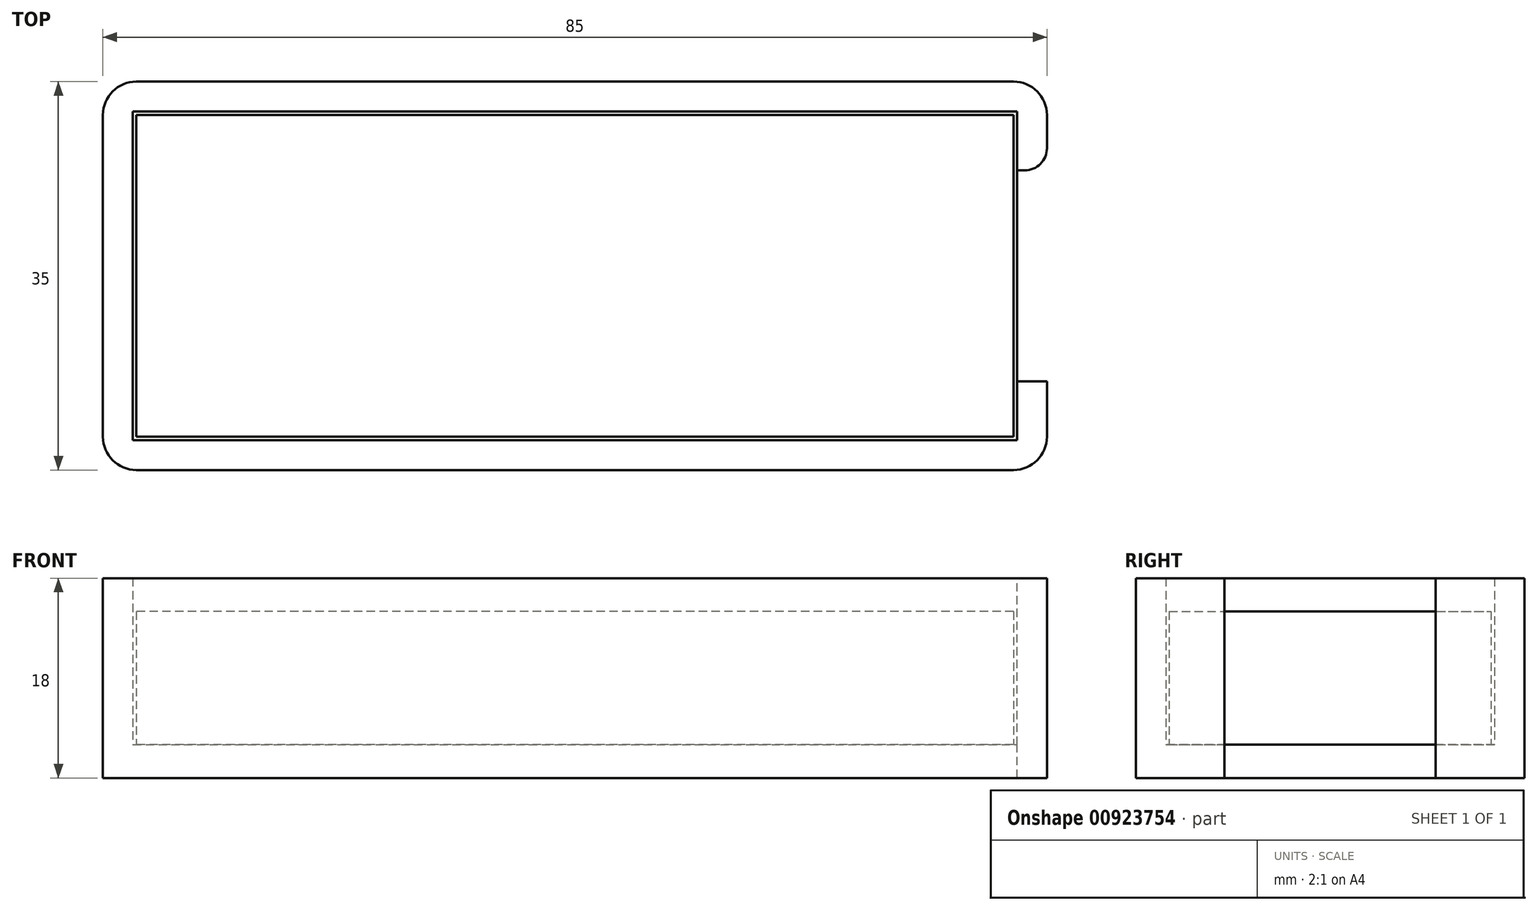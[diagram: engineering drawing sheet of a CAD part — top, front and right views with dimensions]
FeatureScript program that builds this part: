
annotation { "Feature Type Name" : "Feature", "Feature Type Description" : "" }
export const myFeature = defineFeature(function(context is Context, id is Id, definition is map)
    precondition{}
    {
        {
            var Q0;
            Q0=qCreatedBy(makeId("Top.planeOp"),FACE);
            var sketch = newSketch(context, id + "F0", { "sketchPlane" : qUnion([Q0])});
            skLineSegment(sketch, "E0.bottom", {"start": v(39.5, -14.5) * mm, "end": v(-39.5, -14.5) * mm});
            skLineSegment(sketch, "E0.top", {"start": v(39.5, 14.5) * mm, "end": v(-39.5, 14.5) * mm});
            skLineSegment(sketch, "E0.left", {"start": v(39.5, -14.5) * mm, "end": v(39.5, 14.5) * mm});
            skLineSegment(sketch, "E0.right", {"start": v(-39.5, -14.5) * mm, "end": v(-39.5, 14.5) * mm});
            skPoint(sketch, "E0.middle", {"position": v(0, 0) * mm});
            skSolve(sketch);
        }
        {
            var Q0;
            Q0 = qSketchRegion(id + "F0", true);
            extrude(context, id + "F1", {"entities" : qUnion([Q0]), "depth" : 12 * mm, "offsetDistance" : 25 * mm});
        }
        {
            var Q0;
            Q0=qCreatedBy(makeId("Top.planeOp"),FACE);
            var sketch = newSketch(context, id + "F2", { "sketchPlane" : qUnion([Q0])});
            skLineSegment(sketch, "E1.bottom", {"start": v(42.5, -17.5) * mm, "end": v(-42.5, -17.5) * mm});
            skLineSegment(sketch, "E1.top", {"start": v(42.5, 17.5) * mm, "end": v(-42.5, 17.5) * mm});
            skLineSegment(sketch, "E1.left", {"start": v(42.5, -17.5) * mm, "end": v(42.5, 17.5) * mm});
            skLineSegment(sketch, "E1.right", {"start": v(-42.5, -17.5) * mm, "end": v(-42.5, 17.5) * mm});
            skPoint(sketch, "E1.middle", {"position": v(0, 0) * mm});
            skLineSegment(sketch, "E2.bottom", {"start": v(-39.5, -14.5) * mm, "end": v(39.5, -14.5) * mm});
            skLineSegment(sketch, "E2.top", {"start": v(-39.5, 14.5) * mm, "end": v(39.5, 14.5) * mm});
            skLineSegment(sketch, "E2.left", {"start": v(-39.5, -14.5) * mm, "end": v(-39.5, 14.5) * mm});
            skLineSegment(sketch, "E2.right", {"start": v(39.5, -14.5) * mm, "end": v(39.5, 14.5) * mm});
            skLineSegment(sketch, "E3.0", {"start": v(39.8, -14.8) * mm, "end": v(39.8, 14.8) * mm});
            skLineSegment(sketch, "E3.1", {"start": v(-39.8, -14.8) * mm, "end": v(39.8, -14.8) * mm});
            skLineSegment(sketch, "E3.2", {"start": v(-39.8, 14.8) * mm, "end": v(-39.8, -14.8) * mm});
            skLineSegment(sketch, "E3.3", {"start": v(39.8, 14.8) * mm, "end": v(-39.8, 14.8) * mm});
            skSolve(sketch);
        }
        {
            var Q0;
            Q0 = qSketchRegion(id + "F2", true);
            extrude(context, id + "F3", {"entities" : qUnion([Q0]), "depth" : 15 * mm, "offsetDistance" : 25 * mm});
        }
        {
            var Q0;
            Q0=makeQuery(id+"F3.opExtrude","CAP_FACE",FACE,{"disambiguationData":[OSD([sQuery(id+"F2.wireOp",EDGE,"E1.bottom"),sQuery(id+"F2.wireOp",EDGE,"E1.top"),sQuery(id+"F2.wireOp",EDGE,"E1.left"),sQuery(id+"F2.wireOp",EDGE,"E1.right"),sQuery(id+"F2.wireOp",EDGE,"E3.0"),sQuery(id+"F2.wireOp",EDGE,"E3.1"),sQuery(id+"F2.wireOp",EDGE,"E3.2"),sQuery(id+"F2.wireOp",EDGE,"E3.3")])],"isStart":true});
            var sketch = newSketch(context, id + "F4", { "sketchPlane" : qUnion([Q0])});
            skLineSegment(sketch, "E4.bottom", {"start": v(-42.5, -17.5) * mm, "end": v(42.5, -17.5) * mm});
            skLineSegment(sketch, "E4.top", {"start": v(-42.5, 17.5) * mm, "end": v(42.5, 17.5) * mm});
            skLineSegment(sketch, "E4.left", {"start": v(-42.5, -17.5) * mm, "end": v(-42.5, 17.5) * mm});
            skLineSegment(sketch, "E4.right", {"start": v(42.5, -17.5) * mm, "end": v(42.5, 17.5) * mm});
            skPoint(sketch, "E4.middle", {"position": v(0, 0) * mm});
            skSolve(sketch);
        }
        {
            var Q0;
            Q0 = qSketchRegion(id + "F4", true);
            extrude(context, id + "F5", {"entities" : qUnion([Q0]), "operationType" : NewBodyOperationType.ADD, "depth" : 3 * mm, "offsetDistance" : 25 * mm});
        }
        {
            var Q0;
            Q0=makeQuery(id+"F3.opExtrude","CAP_FACE",FACE,{"disambiguationData":[OSD([sQuery(id+"F2.wireOp",EDGE,"E1.bottom"),sQuery(id+"F2.wireOp",EDGE,"E1.top"),sQuery(id+"F2.wireOp",EDGE,"E1.left"),sQuery(id+"F2.wireOp",EDGE,"E1.right"),sQuery(id+"F2.wireOp",EDGE,"E3.0"),sQuery(id+"F2.wireOp",EDGE,"E3.1"),sQuery(id+"F2.wireOp",EDGE,"E3.2"),sQuery(id+"F2.wireOp",EDGE,"E3.3")])],"isStart":false});
            var sketch = newSketch(context, id + "F6", { "sketchPlane" : qUnion([Q0])});
            skLineSegment(sketch, "E5.bottom", {"start": v(42.5, -17.5) * mm, "end": v(39.8, -17.5) * mm});
            skLineSegment(sketch, "E5.top", {"start": v(42.5, -9.5) * mm, "end": v(39.8, -9.5) * mm});
            skLineSegment(sketch, "E5.left", {"start": v(42.5, -17.5) * mm, "end": v(42.5, -9.5) * mm});
            skLineSegment(sketch, "E5.right", {"start": v(39.8, -17.5) * mm, "end": v(39.8, -9.5) * mm});
            skLineSegment(sketch, "E6.MirrorCS", {"start": v(42.5, 17.5) * mm, "end": v(39.8, 17.5) * mm});
            skLineSegment(sketch, "E7.MirrorCS", {"start": v(39.8, 17.5) * mm, "end": v(39.8, 9.5) * mm});
            skLineSegment(sketch, "E8.MirrorCS", {"start": v(42.5, 17.5) * mm, "end": v(42.5, 9.5) * mm});
            skLineSegment(sketch, "E9.MirrorCS", {"start": v(42.5, 9.5) * mm, "end": v(39.8, 9.5) * mm});
            skSolve(sketch);
        }
        {
            var Q0;
            {var subQ0=sQuery(id+"F6.wireOp",EDGE,"E5.top");Q0=makeQuery(id+"F6.imprint","IMPRINT",FACE,{"disambiguationData":[TD([[makeQuery(id+"F6.imprint","IMPRINT",EDGE,{"derivedFrom":subQ0}),-1.0]])]});}
            extrude(context, id + "F7", {"entities" : qUnion([Q0]), "operationType" : NewBodyOperationType.REMOVE, "oppositeDirection" : true, "depth" : 25 * mm, "offsetDistance" : 25 * mm});
        }
        {
            var Q0;
            Q0=makeQuery(id+"F7.boolean.opBoolean","COPY",EDGE,{"derivedFrom":makeQuery(id+"F7.opExtrude","SWEPT_EDGE",EDGE,{"disambiguationData":[OSD([sQuery(id+"F2.wireOp",EDGE,"E1.left"),sQuery(id+"F6.wireOp",EDGE,"E5.top"),sQuery(id+"F6.wireOp",EDGE,"E5.left")])]})});
            var Q1;
            Q1=makeQuery(id+"F7.boolean.opBoolean","COPY",EDGE,{"derivedFrom":makeQuery(id+"F7.opExtrude","SWEPT_EDGE",EDGE,{"disambiguationData":[OSD([sQuery(id+"F2.wireOp",EDGE,"E1.left"),sQuery(id+"F6.wireOp",EDGE,"E8.MirrorCS"),sQuery(id+"F6.wireOp",EDGE,"E9.MirrorCS")])]})});
            fillet(context, id + "F8", {"entities" : qUnion([Q0, Q1]), "radius" : 2 * mm, "tangentPropagation" : true, "allowEdgeOverflow" : false});
        }
        {
            var Q0;
            Q0=makeQuery(id+"F5.boolean.opBoolean","MERGE",EDGE,{"derivedFrom":[makeQuery(id+"F3.opExtrude","SWEPT_EDGE",EDGE,{"disambiguationData":[OSD([sQuery(id+"F2.wireOp",EDGE,"E1.bottom"),sQuery(id+"F2.wireOp",EDGE,"E1.left")])]}),makeQuery(id+"F5.opExtrude","SWEPT_EDGE",EDGE,{"disambiguationData":[OSD([sQuery(id+"F4.wireOp",EDGE,"E4.top"),sQuery(id+"F4.wireOp",EDGE,"E4.right")])]})]});
            var Q1;
            Q1=makeQuery(id+"F5.boolean.opBoolean","MERGE",EDGE,{"derivedFrom":[makeQuery(id+"F3.opExtrude","SWEPT_EDGE",EDGE,{"disambiguationData":[OSD([sQuery(id+"F2.wireOp",EDGE,"E1.bottom"),sQuery(id+"F2.wireOp",EDGE,"E1.right")])]}),makeQuery(id+"F5.opExtrude","SWEPT_EDGE",EDGE,{"disambiguationData":[OSD([sQuery(id+"F4.wireOp",EDGE,"E4.top"),sQuery(id+"F4.wireOp",EDGE,"E4.left")])]})]});
            var Q2;
            Q2=makeQuery(id+"F5.boolean.opBoolean","MERGE",EDGE,{"derivedFrom":[makeQuery(id+"F3.opExtrude","SWEPT_EDGE",EDGE,{"disambiguationData":[OSD([sQuery(id+"F2.wireOp",EDGE,"E1.top"),sQuery(id+"F2.wireOp",EDGE,"E1.right")])]}),makeQuery(id+"F5.opExtrude","SWEPT_EDGE",EDGE,{"disambiguationData":[OSD([sQuery(id+"F4.wireOp",EDGE,"E4.bottom"),sQuery(id+"F4.wireOp",EDGE,"E4.left")])]})]});
            var Q3;
            Q3=makeQuery(id+"F5.boolean.opBoolean","MERGE",EDGE,{"derivedFrom":[makeQuery(id+"F3.opExtrude","SWEPT_EDGE",EDGE,{"disambiguationData":[OSD([sQuery(id+"F2.wireOp",EDGE,"E1.top"),sQuery(id+"F2.wireOp",EDGE,"E1.left")])]}),makeQuery(id+"F5.opExtrude","SWEPT_EDGE",EDGE,{"disambiguationData":[OSD([sQuery(id+"F4.wireOp",EDGE,"E4.bottom"),sQuery(id+"F4.wireOp",EDGE,"E4.right")])]})]});
            fillet(context, id + "F9", {"entities" : qUnion([Q0, Q1, Q2, Q3]), "radius" : 3 * mm, "tangentPropagation" : true, "allowEdgeOverflow" : false});
        }
    });
